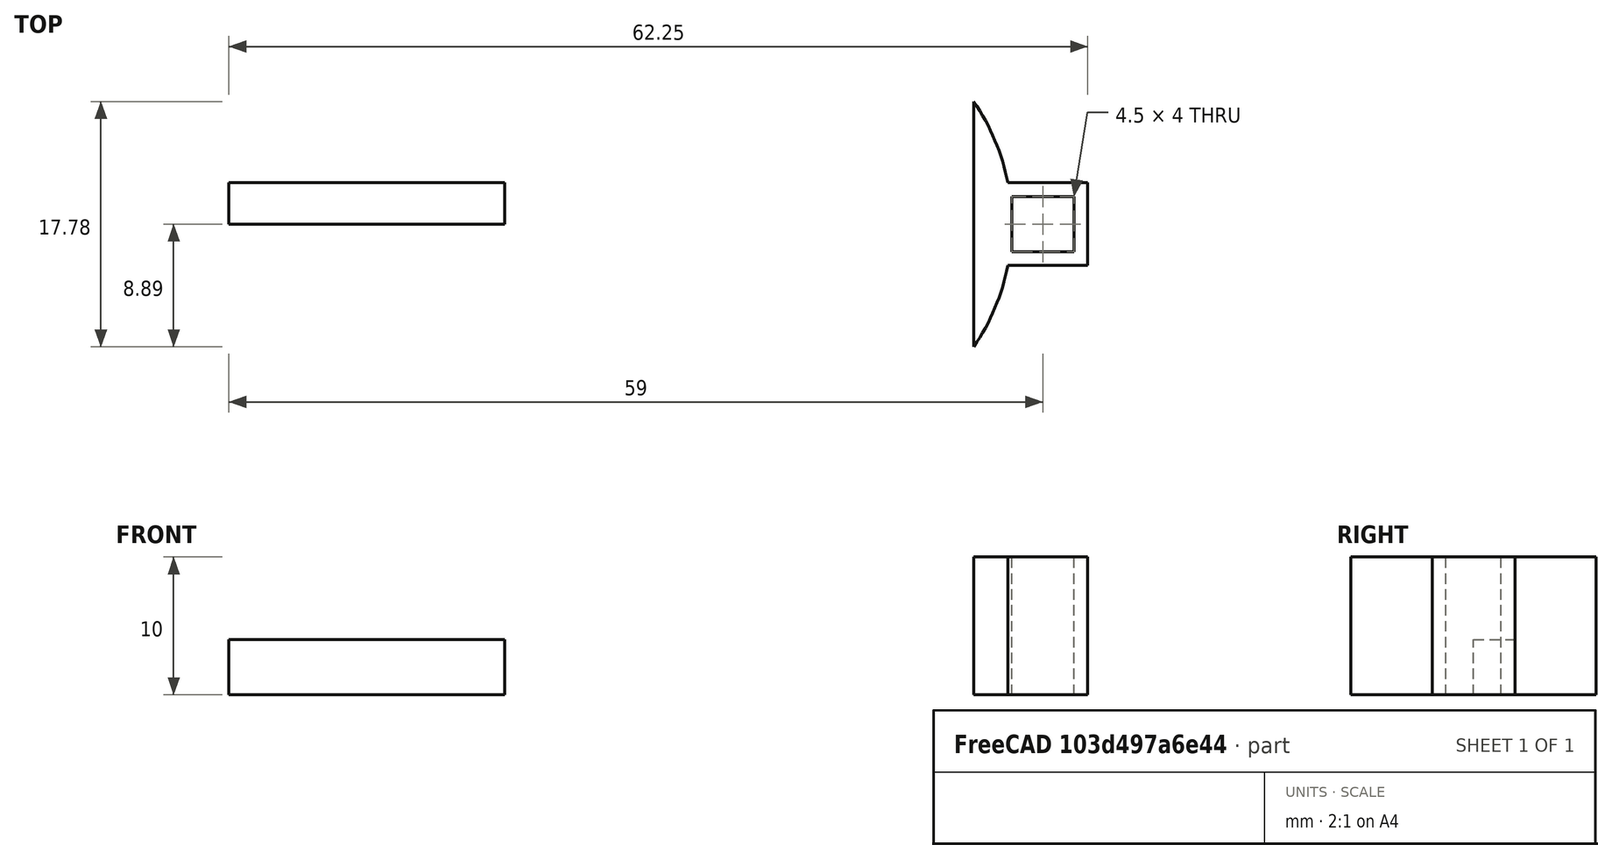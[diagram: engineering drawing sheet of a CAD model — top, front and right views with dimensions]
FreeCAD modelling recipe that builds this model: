
FCSTD DOCUMENT  (FreeCAD 0.19R24267 +99 (Git))
Label: triggerFrameTest
License: All rights reserved
LicenseURL: http://en.wikipedia.org/wiki/All_rights_reserved
objects: PartDesign::AdditiveBox×2, PartDesign::SubtractiveBox×2, PartDesign::Body×2, PartDesign::AdditiveCylinder×1
note: 12 computed .brp shape members not serialized (recipe doc carries the construction recipe); baked Part::Feature solids carry a one-line shape summary decoded from their .brp

FEATURE [PartDesign::AdditiveCylinder] Cylinder
  Angle = 360
  AttacherType = Attacher::AttachEngine3D
  Height = 10
  Radius = 15.75
  Refine = true
FEATURE [PartDesign::AdditiveBox] Box
  AttacherType = Attacher::AttachEngine3D
  AttachmentOffset = pos=(13.75,-3,0) rot=(0,0,1;0rad)
  BaseFeature = -> Cylinder
  Height = 10
  Length = 7.5
  MapMode = 5
  Placement = pos=(13.75,-3,0) rot=(0,0,1;0rad)
  Refine = true
  Support = -> [XY_Plane]
  Width = 6
  expr: .AttachmentOffset.Base.x = Cylinder.Radius - 2mm
  expr: .AttachmentOffset.Base.y = -Width / 2
FEATURE [PartDesign::SubtractiveBox] Box001
  AttacherType = Attacher::AttachEngine3D
  AttachmentOffset = pos=(15.75,-2,0) rot=(0,0,1;0rad)
  BaseFeature = -> Box
  Height = 10
  Length = 4.5
  MapMode = 5
  Placement = pos=(15.75,-2,0) rot=(0,0,1;0rad)
  Refine = true
  Support = -> [XY_Plane]
  Width = 4
  expr: .AttachmentOffset.Base.y = -Width / 2
  expr: .AttachmentOffset.Base.x = Cylinder.Radius
FEATURE [PartDesign::AdditiveBox] Box002
  AttacherType = Attacher::AttachEngine3D
  AttachmentOffset = pos=(-41,0,0) rot=(0,0,1;0rad)
  Height = 4
  Length = 20
  MapMode = 5
  Placement = pos=(-41,0,0) rot=(0,0,1;0rad)
  Refine = true
  Support = -> [XY_Plane001]
  Width = 3
FEATURE [PartDesign::Body] Body001
  Group = -> [Box002]
  Origin = -> Origin001
  Tip = -> Box002
FEATURE [PartDesign::SubtractiveBox] Box003
  AttacherType = Attacher::AttachEngine3D
  AttachmentOffset = pos=(-17,-17,0) rot=(0,0,1;0rad)
  BaseFeature = -> Box001
  Height = 10
  Length = 30
  MapMode = 5
  Placement = pos=(-17,-17,0) rot=(0,0,1;0rad)
  Refine = true
  Support = -> [XY_Plane]
  Width = 35
FEATURE [PartDesign::Body] Body
  Group = -> [Cylinder,Box,Box001,Box003]
  Origin = -> Origin
  Tip = -> Box003
